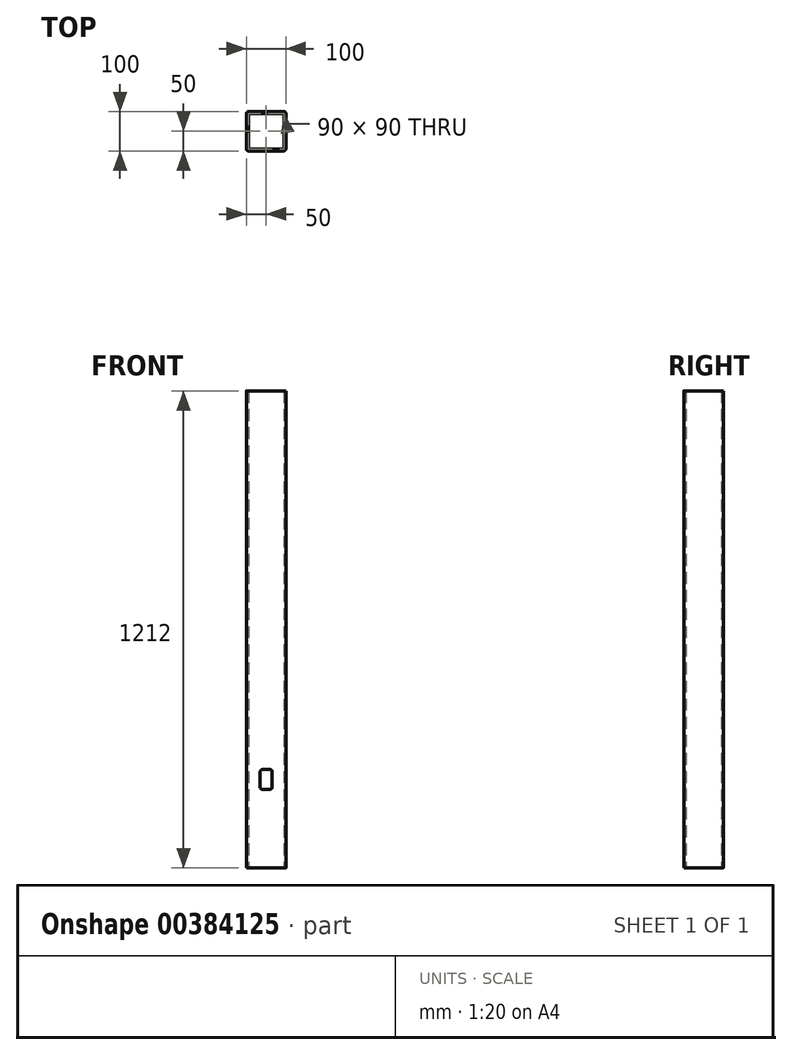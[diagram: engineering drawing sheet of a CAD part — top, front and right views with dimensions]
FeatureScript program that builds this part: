
annotation { "Feature Type Name" : "Feature", "Feature Type Description" : "" }
export const myFeature = defineFeature(function(context is Context, id is Id, definition is map)
    precondition{}
    {
        {
            var Q0;
            Q0=qCreatedBy(makeId("Top.planeOp"),FACE);
            var sketch = newSketch(context, id + "F0", { "sketchPlane" : qUnion([Q0])});
            skLineSegment(sketch, "E0.bottom", {"start": v(45, 50) * mm, "end": v(-45, 50) * mm});
            skLineSegment(sketch, "E0.top", {"start": v(45, -50) * mm, "end": v(-45, -50) * mm});
            skLineSegment(sketch, "E0.left", {"start": v(50, 45) * mm, "end": v(50, -45) * mm});
            skLineSegment(sketch, "E0.right", {"start": v(-50, 45) * mm, "end": v(-50, -45) * mm});
            skPoint(sketch, "E0.middle", {"position": v(0, 0) * mm});
            skPoint(sketch, "E1.visualSharp", {"position": v(-50, 50) * mm});
            skArc(sketch, "E1.filletArc", {"start": v(-45, 50) * mm, "mid": v(-48.54, 48.54) * mm, "end": v(-50, 45) * mm});
            skPoint(sketch, "E2.visualSharp", {"position": v(50, 50) * mm});
            skArc(sketch, "E2.filletArc", {"start": v(50, 45) * mm, "mid": v(48.54, 48.54) * mm, "end": v(45, 50) * mm});
            skPoint(sketch, "E3.visualSharp", {"position": v(-50, -50) * mm});
            skArc(sketch, "E3.filletArc", {"start": v(-50, -45) * mm, "mid": v(-48.54, -48.54) * mm, "end": v(-45, -50) * mm});
            skPoint(sketch, "E4.visualSharp", {"position": v(50, -50) * mm});
            skArc(sketch, "E4.filletArc", {"start": v(45, -50) * mm, "mid": v(48.54, -48.54) * mm, "end": v(50, -45) * mm});
            skLineSegment(sketch, "E5.bottom", {"start": v(45, 45) * mm, "end": v(-45, 45) * mm});
            skLineSegment(sketch, "E5.top", {"start": v(45, -45) * mm, "end": v(-45, -45) * mm});
            skLineSegment(sketch, "E5.left", {"start": v(45, 45) * mm, "end": v(45, -45) * mm});
            skLineSegment(sketch, "E5.right", {"start": v(-45, 45) * mm, "end": v(-45, -45) * mm});
            skSolve(sketch);
        }
        {
            var Q0;
            Q0=makeQuery(id+"F0.imprint","IMPRINT",FACE,{"disambiguationData":[TD([[makeQuery(id+"F0.imprint","IMPRINT",EDGE,{"derivedFrom":sQuery(id+"F0.wireOp",EDGE,"E0.bottom")}),1.0]])]});
            extrude(context, id + "F1", {"entities" : qUnion([Q0]), "depth" : 1212 * mm});
        }
        {
            var Q0;
            Q0=makeQuery(id+"F1.opExtrude","SWEPT_FACE",FACE,{"disambiguationData":[OSD([sQuery(id+"F0.wireOp",EDGE,"E0.top")])]});
            var sketch = newSketch(context, id + "F2", { "sketchPlane" : qUnion([Q0])});
            skLineSegment(sketch, "E6.bottom", {"start": v(-10, 200) * mm, "end": v(10, 200) * mm});
            skLineSegment(sketch, "E6.top", {"start": v(-10, 250) * mm, "end": v(10, 250) * mm});
            skLineSegment(sketch, "E6.left", {"start": v(-15, 205) * mm, "end": v(-15, 245) * mm});
            skLineSegment(sketch, "E6.right", {"start": v(15, 205) * mm, "end": v(15, 245) * mm});
            skPoint(sketch, "E6.middle", {"position": v(0, 225) * mm});
            skPoint(sketch, "E7.visualSharp", {"position": v(-15, 250) * mm});
            skArc(sketch, "E7.filletArc", {"start": v(-10, 250) * mm, "mid": v(-13.54, 248.54) * mm, "end": v(-15, 245) * mm});
            skPoint(sketch, "E8.visualSharp", {"position": v(15, 250) * mm});
            skArc(sketch, "E8.filletArc", {"start": v(15, 245) * mm, "mid": v(13.54, 248.54) * mm, "end": v(10, 250) * mm});
            skPoint(sketch, "E9.visualSharp", {"position": v(15, 200) * mm});
            skArc(sketch, "E9.filletArc", {"start": v(10, 200) * mm, "mid": v(13.54, 201.46) * mm, "end": v(15, 205) * mm});
            skPoint(sketch, "E10.visualSharp", {"position": v(-15, 200) * mm});
            skArc(sketch, "E10.filletArc", {"start": v(-15, 205) * mm, "mid": v(-13.54, 201.46) * mm, "end": v(-10, 200) * mm});
            skSolve(sketch);
        }
        {
            var Q0;
            Q0=qSketchRegion(id+"F2",true);
            var Q1;
            Q1=makeQuery(id+"F2.imprint","IMPRINT",FACE,{"disambiguationData":[TD([[makeQuery(id+"F2.imprint","IMPRINT",EDGE,{"derivedFrom":sQuery(id+"F2.wireOp",EDGE,"E6.bottom")}),1.0]])]});
            extrude(context, id + "F3", {"entities" : qUnion([Q0, Q1]), "operationType" : NewBodyOperationType.REMOVE, "oppositeDirection" : true, "depth" : 4 * mm});
        }
    });
